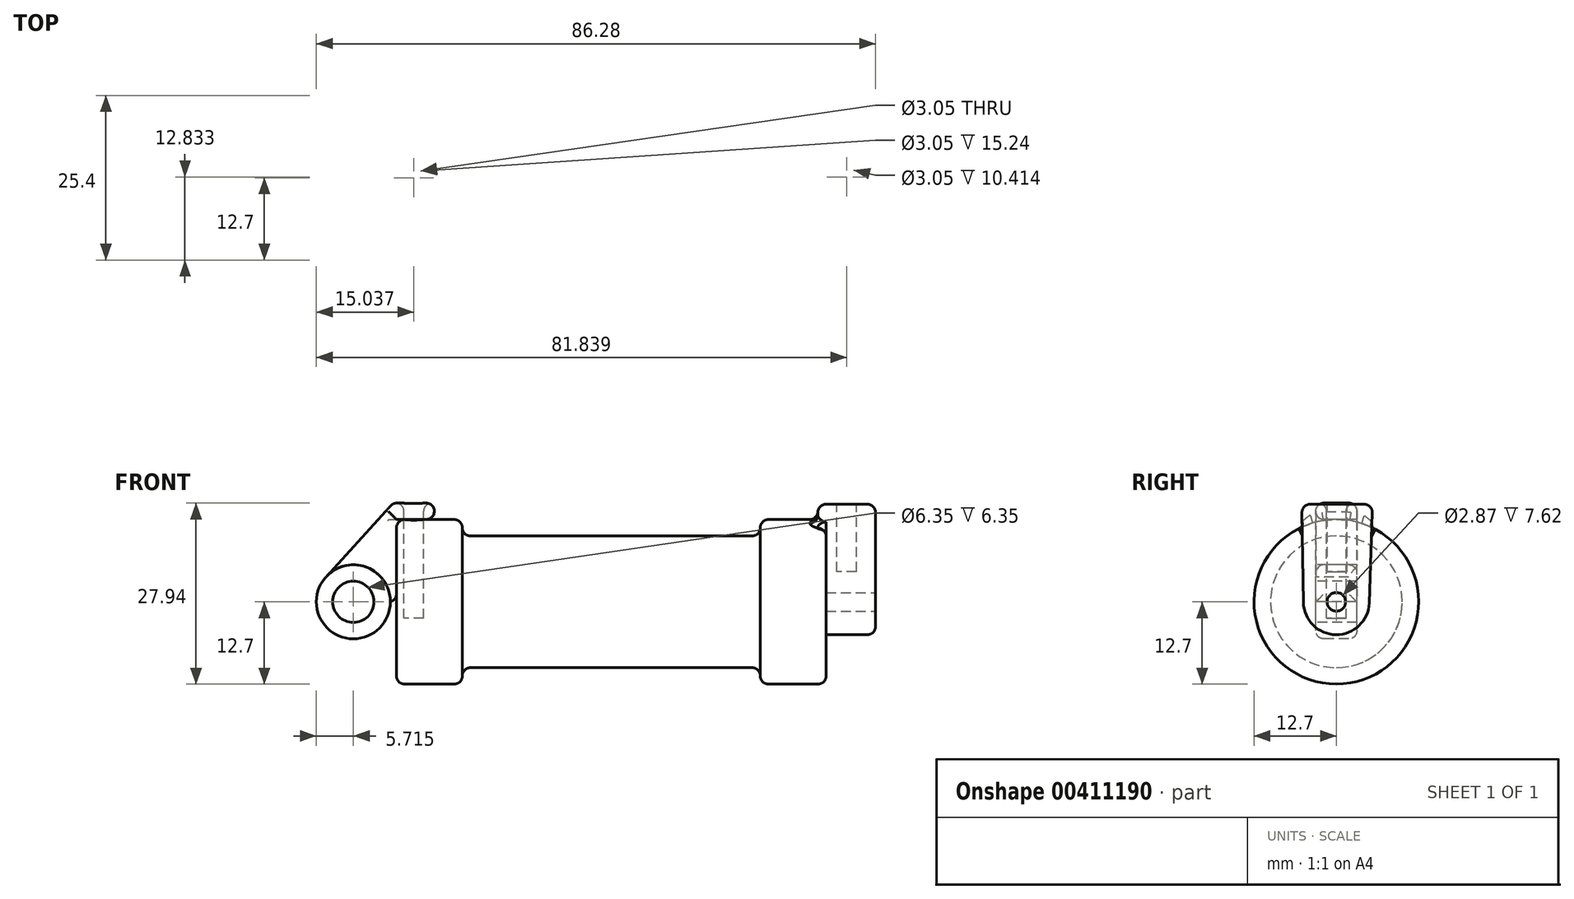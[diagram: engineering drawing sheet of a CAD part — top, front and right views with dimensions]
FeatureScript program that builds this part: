
annotation { "Feature Type Name" : "Feature", "Feature Type Description" : "" }
export const myFeature = defineFeature(function(context is Context, id is Id, definition is map)
    precondition{}
    {
        {
            var Q0;
            Q0=qCreatedBy(makeId("Front.planeOp"),FACE);
            var sketch = newSketch(context, id + "F0", { "sketchPlane" : qUnion([Q0])});
            skLineSegment(sketch, "E0", {"start": v(0, 0) * mm, "end": v(0, 12.7) * mm});
            skLineSegment(sketch, "E1", {"start": v(0, 12.7) * mm, "end": v(10.16, 12.7) * mm});
            skLineSegment(sketch, "E2", {"start": v(10.16, 12.7) * mm, "end": v(10.16, 10.16) * mm});
            skLineSegment(sketch, "E3", {"start": v(10.16, 10.16) * mm, "end": v(56.13, 10.16) * mm});
            skLineSegment(sketch, "E4", {"start": v(56.13, 10.16) * mm, "end": v(56.13, 12.7) * mm});
            skLineSegment(sketch, "E5", {"start": v(56.13, 12.7) * mm, "end": v(66.3, 12.7) * mm});
            skLineSegment(sketch, "E6", {"start": v(66.3, 12.7) * mm, "end": v(66.3, 0) * mm});
            skLineSegment(sketch, "E7", {"start": v(66.3, 0) * mm, "end": v(0, 0) * mm});
            skLineSegment(sketch, "E8", {"start": v(5.84, 15.24) * mm, "end": v(-0.5, 15.24) * mm});
            skLineSegment(sketch, "E9", {"start": v(-0.5, 15.24) * mm, "end": v(-10.88, 3.85) * mm});
            skLineSegment(sketch, "E10", {"start": v(0, 0) * mm, "end": v(-6.65, 0) * mm});
            skCircle(sketch, "E11", {"center": v(-6.65, 0) * mm, "radius": 5.72 * mm});
            skCircle(sketch, "E12", {"center": v(-6.65, 0) * mm, "radius": 3.18 * mm});
            skLineSegment(sketch, "E13", {"start": v(5.84, 15.24) * mm, "end": v(5.84, -9.4) * mm});
            skLineSegment(sketch, "E14", {"start": v(5.84, -9.4) * mm, "end": v(-8.18, -5.5) * mm});
            skSolve(sketch);
        }
        {
            var Q0;
            {var subQ0=sQuery(id+"F0.wireOp",EDGE,"E0");Q0=makeQuery(id+"F0.imprint","IMPRINT",FACE,{"disambiguationData":[TD([[makeQuery(id+"F0.imprint","IMPRINT",EDGE,{"derivedFrom":subQ0}),-1.0]])]});}
            var Q1;
            {var subQ0=sQuery(id+"F0.wireOp",EDGE,"E2");Q1=makeQuery(id+"F0.imprint","IMPRINT",FACE,{"disambiguationData":[TD([[makeQuery(id+"F0.imprint","IMPRINT",EDGE,{"derivedFrom":subQ0}),-1.0]])]});}
            var Q2;
            Q2=sQuery(id+"F0.wireOp",EDGE,"E7");
            revolve(context, id + "F1", {"entities" : qUnion([Q0, Q1]), "axis" : qUnion([Q2]), "revolveType" : RevolveType.FULL});
        }
        {
            var Q0;
            {var subQ5=sQuery(id+"F0.wireOp",EDGE,"E12");Q0=makeQuery(id+"F0.imprint","IMPRINT",FACE,{"disambiguationData":[TD([[makeQuery(id+"F0.imprint","IMPRINT",EDGE,{"derivedFrom":subQ5}),-1.0]])]});}
            extrude(context, id + "F2", {"entities" : qUnion([Q0]), "endBound" : BoundingType.SYMMETRIC, "oppositeDirection" : true, "depth" : 6.35 * mm});
        }
        {
            var Q0;
            {var subQ1=sQuery(id+"F0.wireOp",EDGE,"E0");Q0=makeQuery(id+"F0.imprint","IMPRINT",FACE,{"disambiguationData":[TD([[makeQuery(id+"F0.imprint","IMPRINT",EDGE,{"derivedFrom":subQ1}),1.0]])]});}
            extrude(context, id + "F3", {"entities" : qUnion([Q0]), "endBound" : BoundingType.SYMMETRIC, "oppositeDirection" : true, "depth" : 6.35 * mm});
        }
        {
            var Q0;
            Q0=makeQuery(id+"F1.opRevolve","SWEPT_FACE",FACE,{"disambiguationData":[OSD([sQuery(id+"F0.wireOp",EDGE,"E6")])]});
            var sketch = newSketch(context, id + "F4", { "sketchPlane" : qUnion([Q0])});
            skCircle(sketch, "E15", {"center": v(0, 0) * mm, "radius": 1.52 * mm});
            skCircle(sketch, "E16", {"center": v(0, 0) * mm, "radius": 5.08 * mm});
            skLineSegment(sketch, "E17", {"start": v(-5.08, -0.08) * mm, "end": v(-5.33, 15.06) * mm});
            skLineSegment(sketch, "E18", {"start": v(-5.33, 15.06) * mm, "end": v(5.6, 15.06) * mm});
            skLineSegment(sketch, "E19", {"start": v(5.6, 15.06) * mm, "end": v(5.08, -0.17) * mm});
            skSolve(sketch);
        }
        {
            var Q0;
            {var subQ0=sQuery(id+"F4.wireOp",EDGE,"E17");var subQ1=sQuery(id+"F4.wireOp",EDGE,"E16");var subQ2=makeQuery(id+"F4.imprint","INTERSECT",VERTEX,{"derivedFrom":[subQ1,subQ0]});Q0=makeQuery(id+"F4.imprint","IMPRINT",FACE,{"disambiguationData":[TD([[makeQuery(id+"F4.imprint","IMPRINT",EDGE,{"disambiguationData":[TD([[subQ2,1.0]])],"derivedFrom":subQ1}),-1.0]])]});}
            var Q1;
            {var subQ0=sQuery(id+"F4.wireOp",EDGE,"E18");Q1=makeQuery(id+"F4.imprint","IMPRINT",FACE,{"disambiguationData":[TD([[makeQuery(id+"F4.imprint","IMPRINT",EDGE,{"derivedFrom":subQ0}),-1.0]])]});}
            var Q2;
            Q2=makeQuery(id+"F4.imprint","IMPRINT",FACE,{"disambiguationData":[TD([[makeQuery(id+"F4.imprint","IMPRINT",EDGE,{"derivedFrom":sQuery(id+"F4.wireOp",EDGE,"E15")}),-1.0]])]});
            var Q3;
            Q3=makeQuery(id+"F4.imprint","IMPRINT",FACE,{"disambiguationData":[TD([[makeQuery(id+"F4.imprint","IMPRINT",EDGE,{"derivedFrom":sQuery(id+"F4.wireOp",EDGE,"E15")}),1.0]])]});
            extrude(context, id + "F5", {"entities" : qUnion([Q0, Q1, Q2, Q3]), "operationType" : NewBodyOperationType.ADD, "depth" : 7.62 * mm});
        }
        {
            var Q0;
            Q0=makeQuery(id+"F5.opExtrude","CAP_FACE",FACE,{"disambiguationData":[OSD([sQuery(id+"F4.wireOp",EDGE,"E16"),sQuery(id+"F4.wireOp",EDGE,"E17"),sQuery(id+"F4.wireOp",EDGE,"E18"),sQuery(id+"F4.wireOp",EDGE,"E19")])],"isStart":true});
            extrude(context, id + "F6", {"entities" : qUnion([Q0]), "operationType" : NewBodyOperationType.ADD, "depth" : 1.27 * mm});
        }
        {
            var Q0;
            Q0=makeQuery(id+"F5.opExtrude","CAP_FACE",FACE,{"disambiguationData":[OSD([sQuery(id+"F4.wireOp",EDGE,"E16"),sQuery(id+"F4.wireOp",EDGE,"E17"),sQuery(id+"F4.wireOp",EDGE,"E18"),sQuery(id+"F4.wireOp",EDGE,"E19")])],"isStart":false});
            var sketch = newSketch(context, id + "F7", { "sketchPlane" : qUnion([Q0])});
            skCircle(sketch, "E20", {"center": v(0, 0) * mm, "radius": 1.43 * mm});
            skSolve(sketch);
        }
        {
            var Q0;
            Q0=makeQuery(id+"F7.imprint","IMPRINT",FACE,{"disambiguationData":[TD([[makeQuery(id+"F7.imprint","IMPRINT",EDGE,{"derivedFrom":sQuery(id+"F7.wireOp",EDGE,"E20")}),1.0]])]});
            var Q1;
            Q1=sQuery(id+"F4.wireOp",EDGE,"E15");
            extrude(context, id + "F8", {"entities" : qUnion([Q0]), "operationType" : NewBodyOperationType.REMOVE, "surfaceEntities" : qUnion([Q1]), "oppositeDirection" : true, "depth" : 7.62 * mm});
        }
        {
            var Q0;
            Q0=makeQuery(id+"F3.opExtrude","SWEPT_FACE",FACE,{"disambiguationData":[OSD([sQuery(id+"F0.wireOp",EDGE,"E8")])]});
            var sketch = newSketch(context, id + "F9", { "sketchPlane" : qUnion([Q0])});
            skCircle(sketch, "E21", {"center": v(2.67, 0) * mm, "radius": 1.52 * mm});
            skPoint(sketch, "E21.centerSnap0", {"position": v(5.84, 0) * mm});
            skSolve(sketch);
        }
        {
            var Q0;
            Q0=makeQuery(id+"F9.imprint","IMPRINT",FACE,{"disambiguationData":[TD([[makeQuery(id+"F9.imprint","IMPRINT",EDGE,{"derivedFrom":sQuery(id+"F9.wireOp",EDGE,"E21")}),1.0]])]});
            extrude(context, id + "F10", {"entities" : qUnion([Q0]), "operationType" : NewBodyOperationType.REMOVE, "oppositeDirection" : true, "depth" : 17.78 * mm});
        }
        {
            var Q0;
            {var subQ0=sQuery(id+"F4.wireOp",EDGE,"E18");Q0=makeQuery(id+"F6.boolean.opBoolean","MERGE",FACE,{"derivedFrom":[makeQuery(id+"F5.opExtrude","SWEPT_FACE",FACE,{"disambiguationData":[OSD([subQ0])]}),makeQuery(id+"F6.opExtrude","SWEPT_FACE",FACE,{"disambiguationData":[OSD([subQ0])]})]});}
            var sketch = newSketch(context, id + "F11", { "sketchPlane" : qUnion([Q0])});
            skCircle(sketch, "E22", {"center": v(69.47, 0.13) * mm, "radius": 1.52 * mm});
            skSolve(sketch);
        }
        {
            var Q0;
            Q0=makeQuery(id+"F11.imprint","IMPRINT",FACE,{"disambiguationData":[TD([[makeQuery(id+"F11.imprint","IMPRINT",EDGE,{"derivedFrom":sQuery(id+"F11.wireOp",EDGE,"E22")}),1.0]])]});
            extrude(context, id + "F12", {"entities" : qUnion([Q0]), "operationType" : NewBodyOperationType.REMOVE, "oppositeDirection" : true, "depth" : 10.4 * mm});
        }
        {
            var Q0;
            Q0=makeQuery(id+"F1.opRevolve","SWEPT_EDGE",EDGE,{"disambiguationData":[OSD([sQuery(id+"F0.wireOp",EDGE,"E1"),sQuery(id+"F0.wireOp",EDGE,"E2")])]});
            fillet(context, id + "F13", {"entities" : qUnion([Q0]), "radius" : 1.27 * mm, "tangentPropagation" : true, "allowEdgeOverflow" : false});
        }
        {
            var Q0;
            Q0=makeQuery(id+"F1.opRevolve","SWEPT_EDGE",EDGE,{"disambiguationData":[OSD([sQuery(id+"F0.wireOp",EDGE,"E4"),sQuery(id+"F0.wireOp",EDGE,"E5")])]});
            var Q1;
            Q1=makeQuery(id+"F1.opRevolve","SWEPT_EDGE",EDGE,{"disambiguationData":[OSD([sQuery(id+"F0.wireOp",EDGE,"E0"),sQuery(id+"F0.wireOp",EDGE,"E1")])]});
            var Q2;
            Q2=makeQuery(id+"F3.opExtrude","SWEPT_EDGE",EDGE,{"disambiguationData":[OSD([sQuery(id+"F0.wireOp",EDGE,"E8"),sQuery(id+"F0.wireOp",EDGE,"E9")])]});
            var Q3;
            Q3=makeQuery(id+"F3.opExtrude","CAP_EDGE",EDGE,{"disambiguationData":[OSD([sQuery(id+"F0.wireOp",EDGE,"E9")])],"isStart":false});
            var Q4;
            Q4=makeQuery(id+"F2.opExtrude","CAP_EDGE",EDGE,{"disambiguationData":[OSD([sQuery(id+"F0.wireOp",EDGE,"E11")])],"isStart":false});
            var Q5;
            Q5=makeQuery(id+"F2.opExtrude","CAP_EDGE",EDGE,{"disambiguationData":[OSD([sQuery(id+"F0.wireOp",EDGE,"E11")])],"isStart":true});
            var Q6;
            Q6=makeQuery(id+"F3.opExtrude","CAP_EDGE",EDGE,{"disambiguationData":[OSD([sQuery(id+"F0.wireOp",EDGE,"E8")])],"isStart":true});
            var Q7;
            Q7=makeQuery(id+"F3.opExtrude","SWEPT_EDGE",EDGE,{"disambiguationData":[OSD([sQuery(id+"F0.wireOp",EDGE,"E8"),sQuery(id+"F0.wireOp",EDGE,"E13")])]});
            var Q8;
            Q8=makeQuery(id+"F3.opExtrude","SWEPT_FACE",FACE,{"disambiguationData":[OSD([sQuery(id+"F0.wireOp",EDGE,"E8")])]});
            var Q9;
            Q9=makeQuery(id+"F3.opExtrude","CAP_EDGE",EDGE,{"disambiguationData":[OSD([sQuery(id+"F0.wireOp",EDGE,"E1")])],"isStart":true});
            var Q10;
            Q10=makeQuery(id+"F3.opExtrude","SWEPT_EDGE",EDGE,{"disambiguationData":[OSD([sQuery(id+"F0.wireOp",EDGE,"E1"),sQuery(id+"F0.wireOp",EDGE,"E13")])]});
            fillet(context, id + "F14", {"entities" : qUnion([Q0, Q1, Q2, Q3, Q4, Q5, Q6, Q7, Q8, Q9, Q10]), "radius" : 1.27 * mm, "tangentPropagation" : true, "allowEdgeOverflow" : false});
        }
        {
            var Q0;
            Q0=makeQuery(id+"F1.opRevolve","SWEPT_EDGE",EDGE,{"disambiguationData":[OSD([sQuery(id+"F0.wireOp",EDGE,"E2"),sQuery(id+"F0.wireOp",EDGE,"E3")])]});
            fillet(context, id + "F15", {"entities" : qUnion([Q0]), "radius" : 1.27 * mm, "tangentPropagation" : true, "allowEdgeOverflow" : false});
        }
        {
            var Q0;
            Q0=makeQuery(id+"F1.opRevolve","SWEPT_EDGE",EDGE,{"disambiguationData":[OSD([sQuery(id+"F0.wireOp",EDGE,"E3"),sQuery(id+"F0.wireOp",EDGE,"E4")])]});
            fillet(context, id + "F16", {"entities" : qUnion([Q0]), "radius" : 1.27 * mm, "tangentPropagation" : true, "allowEdgeOverflow" : false});
        }
        {
            var Q0;
            Q0=makeQuery(id+"F6.opExtrude","CAP_EDGE",EDGE,{"disambiguationData":[OSD([sQuery(id+"F4.wireOp",EDGE,"E17")])],"isStart":false});
            var Q1;
            {var subQ0=sQuery(id+"F4.wireOp",EDGE,"E18");var subQ1=sQuery(id+"F4.wireOp",EDGE,"E17");Q1=makeQuery(id+"F6.boolean.opBoolean","MERGE",EDGE,{"derivedFrom":[makeQuery(id+"F5.opExtrude","SWEPT_EDGE",EDGE,{"disambiguationData":[OSD([subQ1,subQ0])]}),makeQuery(id+"F6.opExtrude","SWEPT_EDGE",EDGE,{"disambiguationData":[OSD([subQ1,subQ0])]})]});}
            var Q2;
            Q2=makeQuery(id+"F5.opExtrude","CAP_EDGE",EDGE,{"disambiguationData":[OSD([sQuery(id+"F4.wireOp",EDGE,"E17")])],"isStart":false});
            var Q3;
            {var subQ0=sQuery(id+"F4.wireOp",EDGE,"E17");Q3=makeQuery(id+"F5.boolean.opBoolean","SPLIT",EDGE,{"disambiguationData":[topologyDisambiguationEdgeConnected([makeQuery(id+"F1.opRevolve","SWEPT_FACE",FACE,{"disambiguationData":[OSD([sQuery(id+"F0.wireOp",EDGE,"E6")])]})])],"derivedFrom":makeQuery(id+"F5.opExtrude","CAP_EDGE",EDGE,{"disambiguationData":[OSD([subQ0])],"isStart":true})});}
            var Q4;
            Q4=makeQuery(id+"F5.opExtrude","CAP_EDGE",EDGE,{"disambiguationData":[OSD([sQuery(id+"F4.wireOp",EDGE,"E16")])],"isStart":false});
            var Q5;
            Q5=makeQuery(id+"F5.opExtrude","CAP_EDGE",EDGE,{"disambiguationData":[OSD([sQuery(id+"F4.wireOp",EDGE,"E16")])],"isStart":true});
            var Q6;
            Q6=makeQuery(id+"F5.opExtrude","CAP_EDGE",EDGE,{"disambiguationData":[OSD([sQuery(id+"F4.wireOp",EDGE,"E19")])],"isStart":false});
            var Q7;
            Q7=makeQuery(id+"F5.opExtrude","CAP_EDGE",EDGE,{"disambiguationData":[OSD([sQuery(id+"F4.wireOp",EDGE,"E18")])],"isStart":false});
            var Q8;
            Q8=makeQuery(id+"F6.opExtrude","CAP_EDGE",EDGE,{"disambiguationData":[OSD([sQuery(id+"F4.wireOp",EDGE,"E18")])],"isStart":false});
            var Q9;
            {var subQ0=sQuery(id+"F4.wireOp",EDGE,"E19");var subQ1=sQuery(id+"F4.wireOp",EDGE,"E18");Q9=makeQuery(id+"F6.boolean.opBoolean","MERGE",EDGE,{"derivedFrom":[makeQuery(id+"F5.opExtrude","SWEPT_EDGE",EDGE,{"disambiguationData":[OSD([subQ1,subQ0])]}),makeQuery(id+"F6.opExtrude","SWEPT_EDGE",EDGE,{"disambiguationData":[OSD([subQ1,subQ0])]})]});}
            var Q10;
            Q10=makeQuery(id+"F6.opExtrude","CAP_EDGE",EDGE,{"disambiguationData":[OSD([sQuery(id+"F4.wireOp",EDGE,"E19")])],"isStart":false});
            var Q11;
            {var subQ0=sQuery(id+"F4.wireOp",EDGE,"E19");Q11=makeQuery(id+"F5.boolean.opBoolean","SPLIT",EDGE,{"disambiguationData":[topologyDisambiguationEdgeConnected([makeQuery(id+"F1.opRevolve","SWEPT_FACE",FACE,{"disambiguationData":[OSD([sQuery(id+"F0.wireOp",EDGE,"E6")])]})])],"derivedFrom":makeQuery(id+"F5.opExtrude","CAP_EDGE",EDGE,{"disambiguationData":[OSD([subQ0])],"isStart":true})});}
            fillet(context, id + "F17", {"entities" : qUnion([Q0, Q1, Q2, Q3, Q4, Q5, Q6, Q7, Q8, Q9, Q10, Q11]), "radius" : 1.27 * mm, "tangentPropagation" : true, "allowEdgeOverflow" : false});
        }
        {
            var Q0;
            Q0=makeQuery(id+"F6.opExtrude","CAP_EDGE",EDGE,{"disambiguationData":[OSD([sQuery(id+"F0.wireOp",EDGE,"E5"),sQuery(id+"F0.wireOp",EDGE,"E6")])],"isStart":false});
            var Q1;
            Q1=makeQuery(id+"F17.opFillet","BLEND_EDGE",EDGE,{"blendedFrom":[makeQuery(id+"F6.opExtrude","CAP_EDGE",EDGE,{"disambiguationData":[OSD([sQuery(id+"F4.wireOp",EDGE,"E19")])],"isStart":false}),makeQuery(id+"F1.opRevolve","SWEPT_FACE",FACE,{"disambiguationData":[OSD([sQuery(id+"F0.wireOp",EDGE,"E5")])]})],"blendedInto":[makeQuery(id+"F1.opRevolve","SWEPT_FACE",FACE,{"disambiguationData":[OSD([sQuery(id+"F0.wireOp",EDGE,"E5")])]})]});
            var Q2;
            Q2=makeQuery(id+"F17.opFillet","BLEND_EDGE",EDGE,{"blendedFrom":[makeQuery(id+"F6.opExtrude","CAP_EDGE",EDGE,{"disambiguationData":[OSD([sQuery(id+"F4.wireOp",EDGE,"E17")])],"isStart":false}),makeQuery(id+"F1.opRevolve","SWEPT_FACE",FACE,{"disambiguationData":[OSD([sQuery(id+"F0.wireOp",EDGE,"E5")])]})],"blendedInto":[makeQuery(id+"F1.opRevolve","SWEPT_FACE",FACE,{"disambiguationData":[OSD([sQuery(id+"F0.wireOp",EDGE,"E5")])]})]});
            var Q3;
            {var subQ0=sQuery(id+"F0.wireOp",EDGE,"E1");Q3=makeQuery(id+"F14.opFillet","BLEND_EDGE",EDGE,{"blendedFrom":[makeQuery(id+"F3.opExtrude","SWEPT_EDGE",EDGE,{"disambiguationData":[OSD([subQ0,sQuery(id+"F0.wireOp",EDGE,"E13")])]}),makeQuery(id+"F3.opExtrude","SWEPT_FACE",FACE,{"disambiguationData":[OSD([subQ0])]})],"blendedInto":[makeQuery(id+"F3.opExtrude","SWEPT_FACE",FACE,{"disambiguationData":[OSD([subQ0])]})]});}
            fillet(context, id + "F18", {"entities" : qUnion([Q0, Q1, Q2, Q3]), "radius" : 1.27 * mm, "tangentPropagation" : true, "allowEdgeOverflow" : false});
        }
        {
            var Q0;
            Q0=makeQuery(id+"F3.opExtrude","CAP_EDGE",EDGE,{"disambiguationData":[OSD([sQuery(id+"F0.wireOp",EDGE,"E0")])],"isStart":true});
            var Q1;
            Q1=makeQuery(id+"F3.opExtrude","SWEPT_EDGE",EDGE,{"disambiguationData":[OSD([sQuery(id+"F0.wireOp",EDGE,"E0"),sQuery(id+"F0.wireOp",EDGE,"E7"),sQuery(id+"F0.wireOp",EDGE,"E10")])]});
            var Q2;
            Q2=makeQuery(id+"F3.opExtrude","CAP_EDGE",EDGE,{"disambiguationData":[OSD([sQuery(id+"F0.wireOp",EDGE,"E0")])],"isStart":false});
            fillet(context, id + "F19", {"entities" : qUnion([Q0, Q1, Q2]), "radius" : 1.27 * mm, "tangentPropagation" : true, "allowEdgeOverflow" : false});
        }
        {
            var Q0;
            {var subQ0=sQuery(id+"F0.wireOp",EDGE,"E5");var subQ1=sQuery(id+"F0.wireOp",EDGE,"E6");Q0=makeQuery(id+"F5.boolean.opBoolean","SPLIT",EDGE,{"disambiguationData":[topologyDisambiguationEdgeConnected([makeQuery(id+"F1.opRevolve","SWEPT_FACE",FACE,{"disambiguationData":[OSD([subQ1])]})])],"derivedFrom":makeQuery(id+"F1.opRevolve","SWEPT_EDGE",EDGE,{"disambiguationData":[OSD([subQ0,subQ1])]})});}
            fillet(context, id + "F20", {"entities" : qUnion([Q0]), "radius" : 1.27 * mm, "tangentPropagation" : true, "allowEdgeOverflow" : false});
        }
    });
